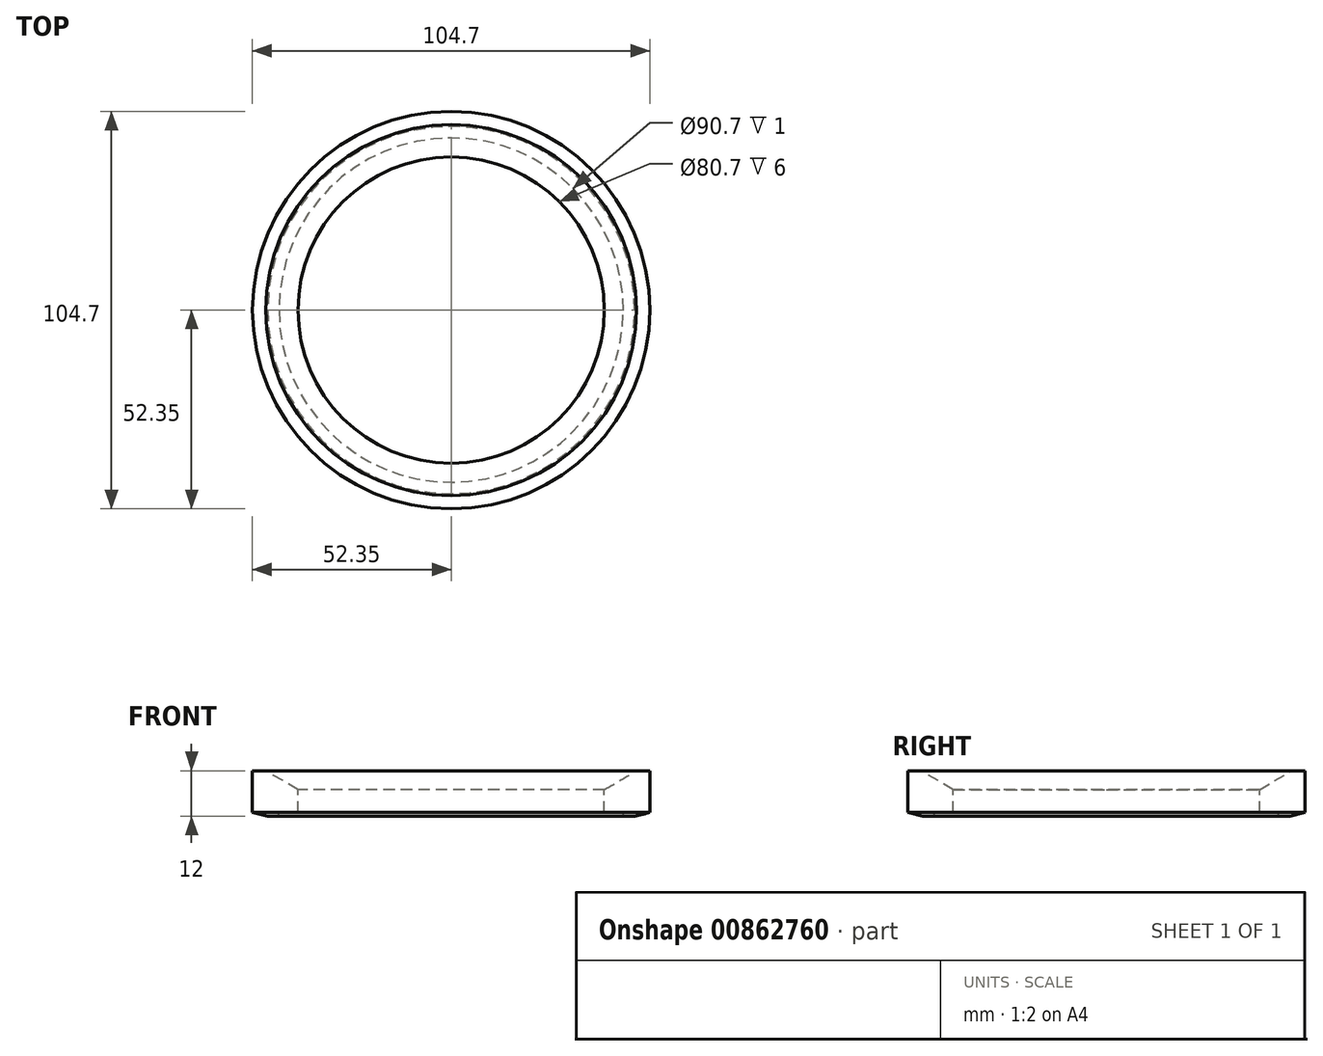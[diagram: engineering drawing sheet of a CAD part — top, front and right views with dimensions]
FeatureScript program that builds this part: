
annotation { "Feature Type Name" : "Feature", "Feature Type Description" : "" }
export const myFeature = defineFeature(function(context is Context, id is Id, definition is map)
    precondition{}
    {
        {
            var Q0;
            Q0=qCreatedBy(makeId("Front.planeOp"),FACE);
            var sketch = newSketch(context, id + "F0", { "sketchPlane" : qUnion([Q0])});
            skLineSegment(sketch, "E0", {"start": v(-48.85, 14.06) * mm, "end": v(-52.35, 14.06) * mm});
            skLineSegment(sketch, "E1", {"start": v(-52.35, 14.06) * mm, "end": v(-52.35, 3.06) * mm});
            skLineSegment(sketch, "E2", {"start": v(-52.35, 3.06) * mm, "end": v(-48.35, 2.06) * mm});
            skLineSegment(sketch, "E3", {"start": v(-48.35, 2.06) * mm, "end": v(-45.35, 2.06) * mm});
            skLineSegment(sketch, "E4", {"start": v(-45.35, 2.06) * mm, "end": v(-45.35, 3.06) * mm});
            skLineSegment(sketch, "E5", {"start": v(-45.35, 3.06) * mm, "end": v(-40.35, 3.06) * mm});
            skLineSegment(sketch, "E6", {"start": v(-40.35, 3.06) * mm, "end": v(-40.35, 9.06) * mm});
            skLineSegment(sketch, "E7", {"start": v(-40.35, 9.06) * mm, "end": v(-48.85, 14.06) * mm});
            skLineSegment(sketch, "E8", {"start": v(0, 49.61) * mm, "end": v(0, -48.8) * mm, "construction": true});
            skSolve(sketch);
        }
        {
            var Q0;
            Q0=makeQuery(id+"F0.imprint","IMPRINT",FACE,{"disambiguationData":[TD([[makeQuery(id+"F0.imprint","IMPRINT",EDGE,{"derivedFrom":sQuery(id+"F0.wireOp",EDGE,"E0")}),1.0]])]});
            var Q1;
            Q1=sQuery(id+"F0.wireOp",EDGE,"E8");
            revolve(context, id + "F1", {"surfaceOperationType" : NewSurfaceOperationType.NEW, "entities" : qUnion([Q0]), "axis" : qUnion([Q1]), "revolveType" : RevolveType.FULL});
        }
    });
